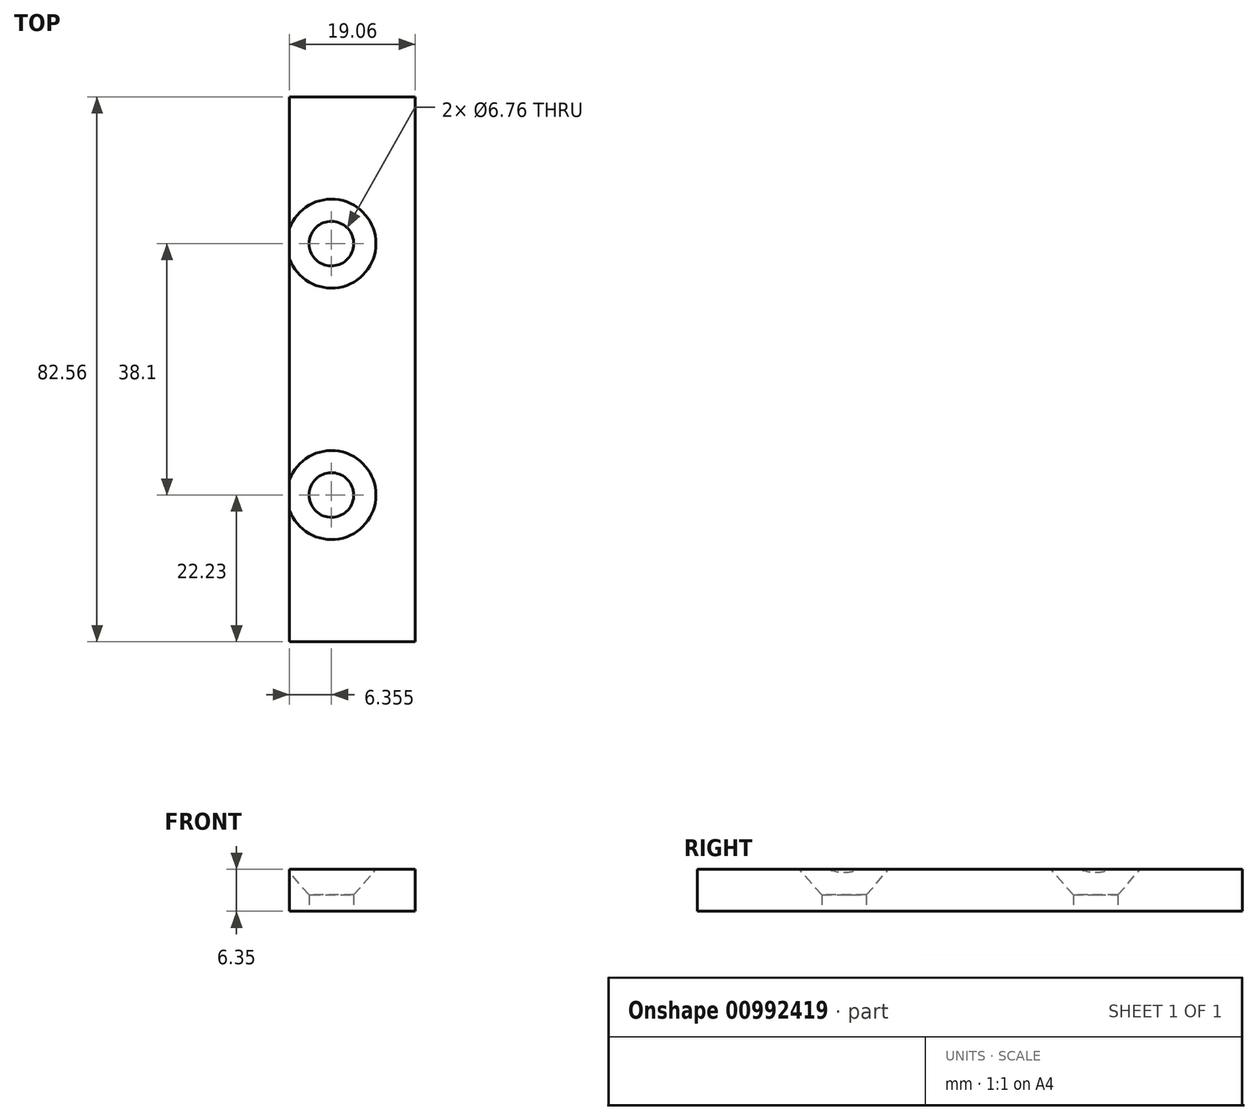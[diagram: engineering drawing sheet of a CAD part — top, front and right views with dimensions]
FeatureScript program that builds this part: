
annotation { "Feature Type Name" : "Feature", "Feature Type Description" : "" }
export const myFeature = defineFeature(function(context is Context, id is Id, definition is map)
    precondition{}
    {
        {
            var Q0;
            Q0=qCreatedBy(makeId("Top.planeOp"),FACE);
            var sketch = newSketch(context, id + "F0", { "sketchPlane" : qUnion([Q0])});
            skLineSegment(sketch, "E0.bottom", {"start": v(9.53, 41.28) * mm, "end": v(-9.52, 41.28) * mm});
            skLineSegment(sketch, "E0.top", {"start": v(9.53, -41.28) * mm, "end": v(-9.52, -41.28) * mm});
            skLineSegment(sketch, "E0.left", {"start": v(9.53, 41.28) * mm, "end": v(9.53, -41.28) * mm});
            skLineSegment(sketch, "E0.right", {"start": v(-9.52, 41.28) * mm, "end": v(-9.52, -41.28) * mm});
            skPoint(sketch, "E0.middle", {"position": v(0, 0) * mm});
            skCircle(sketch, "E1", {"center": v(-3.17, 19.05) * mm, "radius": 3.57 * mm});
            skCircle(sketch, "E2", {"center": v(-3.17, -19.05) * mm, "radius": 3.57 * mm});
            skSolve(sketch);
        }
        {
            var Q0;
            Q0=makeQuery(id+"F0.imprint","IMPRINT",FACE,{"disambiguationData":[TD([[makeQuery(id+"F0.imprint","IMPRINT",EDGE,{"derivedFrom":sQuery(id+"F0.wireOp",EDGE,"E0.bottom")}),1.0]])]});
            var Q1;
            Q1=makeQuery(id+"F0.imprint","IMPRINT",FACE,{"disambiguationData":[TD([[makeQuery(id+"F0.imprint","IMPRINT",EDGE,{"derivedFrom":sQuery(id+"F0.wireOp",EDGE,"E1")}),1.0]])]});
            var Q2;
            Q2=makeQuery(id+"F0.imprint","IMPRINT",FACE,{"disambiguationData":[TD([[makeQuery(id+"F0.imprint","IMPRINT",EDGE,{"derivedFrom":sQuery(id+"F0.wireOp",EDGE,"E2")}),1.0]])]});
            extrude(context, id + "F1", {"entities" : qUnion([Q0, Q1, Q2]), "oppositeDirection" : true, "depth" : 6.35 * mm, "offsetDistance" : 25.4 * mm});
        }
        {
            var Q0;
            Q0=sQuery(id+"F0.wireOp",VERTEX,"E1.center");
            var Q1;
            Q1=sQuery(id+"F0.wireOp",VERTEX,"E2.center");
            var Q2;
            Q2=makeQuery(id+"F1.opExtrude","SWEPT_BODY",BODY,{"disambiguationData":[OSD([sQuery(id+"F0.wireOp",EDGE,"E0.bottom"),sQuery(id+"F0.wireOp",EDGE,"E0.top"),sQuery(id+"F0.wireOp",EDGE,"E0.left"),sQuery(id+"F0.wireOp",EDGE,"E0.right")])]});
            hole(context, id + "F2", {"style" : HoleStyle.C_SINK, "endStyle" : HoleEndStyle.THROUGH, "standardTappedOrClearance" : lookupTablePath({ "fit" : "Close (ASME)", "standard" : "ANSI", "size" : "1/4", "type" : "Clearance" }), "standardBlindInLast" : lookupTablePath({ "fit" : "Close", "standard" : "ANSI", "engagement" : "75%", "pitch" : "20 tpi", "size" : "1/4", "type" : "Clearance & tapped" }), "holeDiameter" : 6.76 * mm, "cSinkDiameter" : 13.5 * mm, "cSinkAngle" : 82 * degree, "majorDiameter" : 6.35 * mm, "isTappedThrough" : true, "tappedDepth" : 12.7 * mm, "tapClearance" : 3, "locations" : qUnion([Q0, Q1]), "scope" : qUnion([Q2]), "startStyle" : HoleStartStyle.SKETCH});
        }
    });
